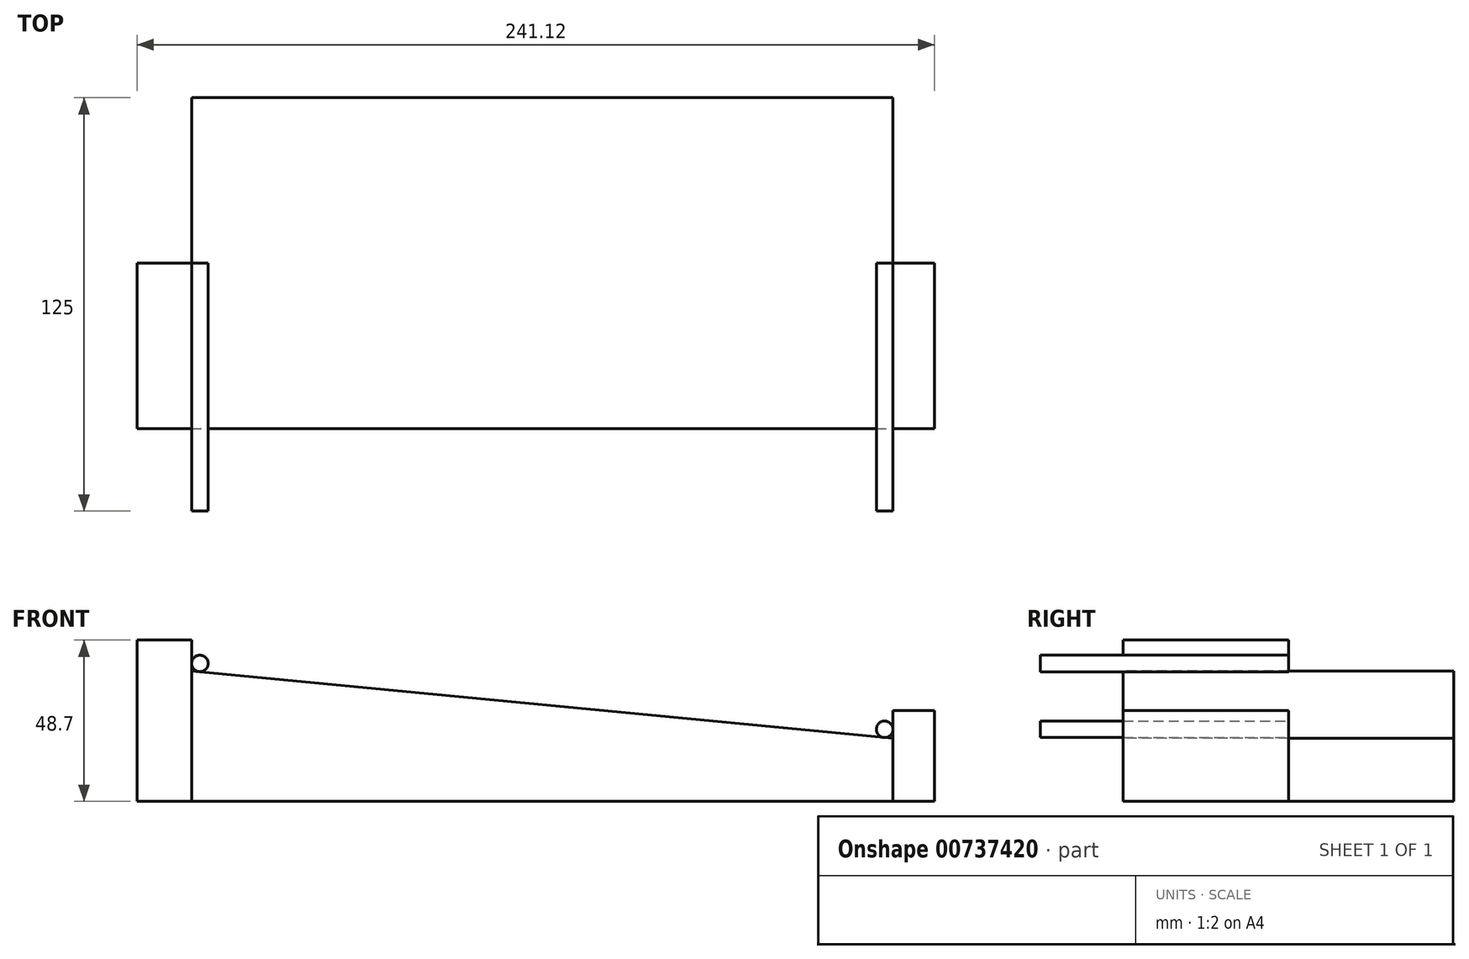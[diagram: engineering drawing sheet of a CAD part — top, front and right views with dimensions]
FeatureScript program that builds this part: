
annotation { "Feature Type Name" : "Feature", "Feature Type Description" : "" }
export const myFeature = defineFeature(function(context is Context, id is Id, definition is map)
    precondition{}
    {
        {
            var Q0;
            Q0=qCreatedBy(makeId("Front.planeOp"),FACE);
            var sketch = newSketch(context, id + "F0", { "sketchPlane" : qUnion([Q0])});
            skLineSegment(sketch, "E0", {"start": v(0, 0) * mm, "end": v(0, 39.4) * mm});
            skLineSegment(sketch, "E1", {"start": v(0, 0) * mm, "end": v(212, 0) * mm});
            skLineSegment(sketch, "E2", {"start": v(0, 39.4) * mm, "end": v(212, 18.99) * mm});
            skLineSegment(sketch, "E3", {"start": v(212, 0) * mm, "end": v(212, 18.99) * mm});
            skLineSegment(sketch, "E4", {"start": v(212, 18.99) * mm, "end": v(212, 85.03) * mm, "construction": true});
            skLineSegment(sketch, "E5", {"start": v(0, 39.4) * mm, "end": v(0, 111.14) * mm, "construction": true});
            skCircle(sketch, "E6", {"center": v(209.5, 21.74) * mm, "radius": 2.5 * mm});
            skCircle(sketch, "E7", {"center": v(2.5, 41.67) * mm, "radius": 2.5 * mm});
            skLineSegment(sketch, "E8", {"start": v(209.5, 21.74) * mm, "end": v(203.4, 21.74) * mm, "construction": true});
            skLineSegment(sketch, "E9.0", {"start": v(218, 24.24) * mm, "end": v(209.5, 24.24) * mm, "construction": true});
            skLineSegment(sketch, "E10", {"start": v(2.5, 41.67) * mm, "end": v(-3.03, 41.67) * mm, "construction": true});
            skLineSegment(sketch, "E11.0", {"start": v(2.5, 44.17) * mm, "end": v(-3.03, 44.17) * mm});
            skSolve(sketch);
        }
        {
            var Q0;
            {var subQ3=sQuery(id+"F0.wireOp",EDGE,"E0");Q0=makeQuery(id+"F0.imprint","IMPRINT",FACE,{"disambiguationData":[TD([[makeQuery(id+"F0.imprint","IMPRINT",EDGE,{"derivedFrom":subQ3}),-1.0]])]});}
            extrude(context, id + "F1", {"entities" : qUnion([Q0]), "oppositeDirection" : true, "depth" : 100 * mm, "offsetDistance" : 25 * mm});
        }
        {
            var Q0;
            {var subQ0=sQuery(id+"F0.wireOp",EDGE,"E7");var subQ1=makeQuery(id+"F0.imprint","IMPRINT",VERTEX,{"derivedFrom":subQ0});Q0=makeQuery(id+"F0.imprint","IMPRINT",FACE,{"disambiguationData":[TD([[makeQuery(id+"F0.imprint","IMPRINT",EDGE,{"disambiguationData":[TD([[subQ1,-1.0]])],"derivedFrom":subQ0}),1.0]])]});}
            var Q1;
            Q1=makeQuery(id+"F0.imprint","IMPRINT",FACE,{"disambiguationData":[TD([[makeQuery(id+"F0.imprint","IMPRINT",EDGE,{"derivedFrom":sQuery(id+"F0.wireOp",EDGE,"E6")}),1.0]])]});
            extrude(context, id + "F2", {"entities" : qUnion([Q0, Q1]), "operationType" : NewBodyOperationType.ADD, "depth" : 25 * mm, "offsetDistance" : 25 * mm, "hasSecondDirection" : true, "secondDirectionOppositeDirection" : true, "secondDirectionDepth" : 50 * mm});
        }
        {
            var Q0;
            {var subQ3=sQuery(id+"F0.wireOp",EDGE,"E0");Q0=makeQuery(id+"F0.imprint","IMPRINT",FACE,{"disambiguationData":[TD([[makeQuery(id+"F0.imprint","IMPRINT",EDGE,{"derivedFrom":subQ3}),-1.0]])]});}
            var sketch = newSketch(context, id + "F3", { "sketchPlane" : qUnion([Q0])});
            skPoint(sketch, "E12.0", {"position": v(212, 0) * mm});
            skPoint(sketch, "E13.0", {"position": v(0, 0) * mm});
            skLineSegment(sketch, "E14.bottom", {"start": v(0, 0) * mm, "end": v(-16.53, 0) * mm});
            skLineSegment(sketch, "E14.top", {"start": v(0, 48.7) * mm, "end": v(-16.53, 48.7) * mm});
            skLineSegment(sketch, "E14.left", {"start": v(0, 0) * mm, "end": v(0, 48.7) * mm});
            skLineSegment(sketch, "E14.right", {"start": v(-16.53, 0) * mm, "end": v(-16.53, 48.7) * mm});
            skLineSegment(sketch, "E15.bottom", {"start": v(212, 0) * mm, "end": v(224.59, 0) * mm});
            skLineSegment(sketch, "E15.top", {"start": v(212, 27.37) * mm, "end": v(224.59, 27.37) * mm});
            skLineSegment(sketch, "E15.left", {"start": v(212, 0) * mm, "end": v(212, 27.37) * mm});
            skLineSegment(sketch, "E15.right", {"start": v(224.59, 0) * mm, "end": v(224.59, 27.37) * mm});
            skSolve(sketch);
        }
        {
            var Q0;
            {var subQ4=sQuery(id+"F3.wireOp",EDGE,"E15.bottom");Q0=makeQuery(id+"F3.imprint","IMPRINT",FACE,{"disambiguationData":[TD([[makeQuery(id+"F3.imprint","IMPRINT",EDGE,{"derivedFrom":subQ4}),1.0]])]});}
            var Q1;
            {var subQ4=sQuery(id+"F3.wireOp",EDGE,"E14.bottom");Q1=makeQuery(id+"F3.imprint","IMPRINT",FACE,{"disambiguationData":[TD([[makeQuery(id+"F3.imprint","IMPRINT",EDGE,{"derivedFrom":subQ4}),-1.0]])]});}
            extrude(context, id + "F4", {"entities" : qUnion([Q0, Q1]), "oppositeDirection" : true, "depth" : 50 * mm, "offsetDistance" : 25 * mm});
        }
    });
